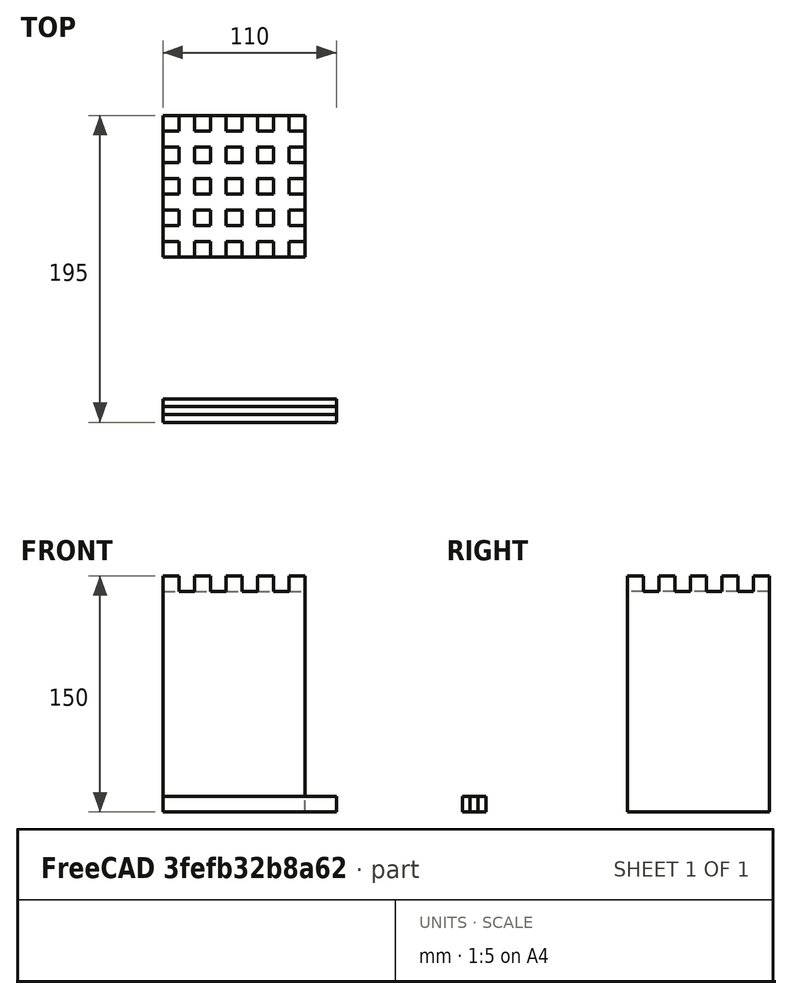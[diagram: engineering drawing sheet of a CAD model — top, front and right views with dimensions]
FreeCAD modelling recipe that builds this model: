
FCSTD DOCUMENT  (FreeCAD 0.21R33694 (Git))
Label: OJT1_T10P03.terror
License: All rights reserved
LicenseURL: http://en.wikipedia.org/wiki/All_rights_reserved
objects: Part::Box×3, Part::FeaturePython×2, Part::Fuse×1, Part::Cut×1
note: 5 computed .brp shape members not serialized (recipe doc carries the construction recipe); baked Part::Feature solids carry a one-line shape summary decoded from their .brp

FEATURE [Part::Box] Box  label="Cub"
  AttacherType = Attacher::AttachEngine3D
  Height = 150
  Length = 90
  Placement = pos=(0,100,0) rot=(0,0,1;0rad)
  Width = 90
FEATURE [Part::Box] Box001  label="Cub001"
  AttacherType = Attacher::AttachEngine3D
  Height = 10
  Length = 110
  Width = 10
FEATURE [Part::FeaturePython] Array  # Draft array (typed FeaturePython)
  AlwaysSyncPlacement = false
  Angle = 360
  ArrayType = 0
  Axis = (0,0,1)
  Base = -> Box001
  Center = (0,0,0)
  Count = 4
  ExpandArray = false
  Fuse = false
  IntervalAxis = (0,0,0)
  IntervalX = (100,0,0)
  IntervalY = (0,20,0)
  IntervalZ = (0,0,100)
  NumberCircles = 3
  NumberPolar = 5
  NumberX = 1
  NumberY = 4
  NumberZ = 1
  PlacementList = 4 placements: arithmetic series from (0,0,0) step (0,20,0) to (0,60,0)
  RadialDistance = 50
  ScaleList = (4) [(1,1,1),(1,1,1),(1,1,1),(1,1,1)]
  Symmetry = 1
  TangentialDistance = 25
FEATURE [Part::Box] Box002  label="Cub002"
  AttacherType = Attacher::AttachEngine3D
  Height = 10
  Length = 110
  Placement = pos=(0,-5,0) rot=(0,0,1;0rad)
  Width = 10
FEATURE [Part::FeaturePython] Array001  # Draft array (typed FeaturePython)
  AlwaysSyncPlacement = false
  Angle = 360
  ArrayType = 0
  Axis = (0,0,1)
  Base = -> Box002
  Center = (0,0,0)
  Count = 4
  ExpandArray = false
  Fuse = false
  IntervalAxis = (0,0,0)
  IntervalX = (100,0,0)
  IntervalY = (0,20,0)
  IntervalZ = (0,0,100)
  NumberCircles = 3
  NumberPolar = 5
  NumberX = 1
  NumberY = 4
  NumberZ = 1
  Placement = pos=(20,90,0) rot=(0,0,-1;1.5708rad)
  PlacementList = 4 placements: arithmetic series from (0,0,0) step (0,20,0) to (0,60,0)
  RadialDistance = 50
  ScaleList = (4) [(1,1,1),(1,1,1),(1,1,1),(1,1,1)]
  Symmetry = 1
  TangentialDistance = 25
FEATURE [Part::Fuse] Fusion
  Base = -> Array
  Placement = pos=(-10,110,140) rot=(0,0,1;0rad)
  Refine = true
  Tool = -> Array001
FEATURE [Part::Cut] Cut
  Base = -> Box
  Refine = true
  Tool = -> Fusion
